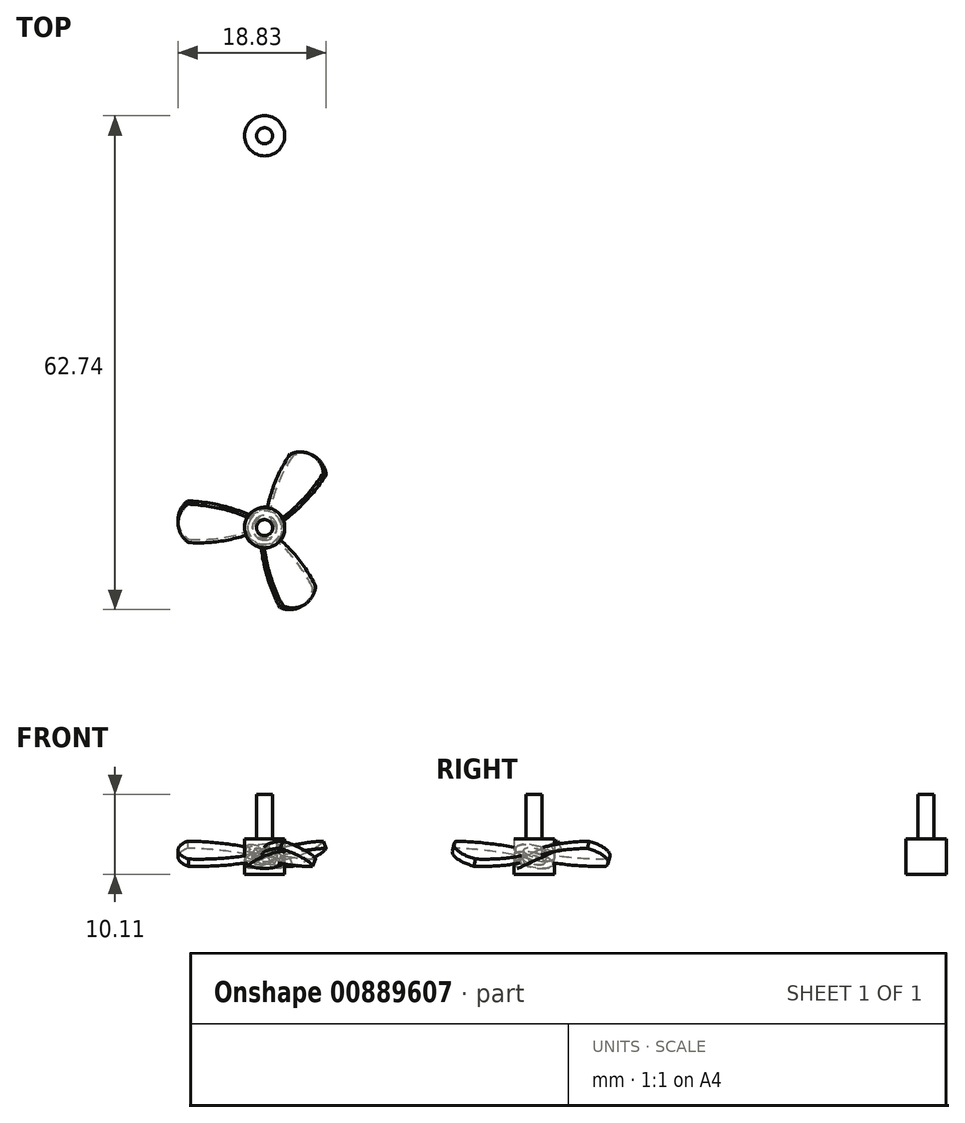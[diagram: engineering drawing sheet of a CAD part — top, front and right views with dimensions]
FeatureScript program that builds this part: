
annotation { "Feature Type Name" : "Feature", "Feature Type Description" : "" }
export const myFeature = defineFeature(function(context is Context, id is Id, definition is map)
    precondition{}
    {
        {
            var Q0;
            Q0=qCreatedBy(makeId("Top.planeOp"),FACE);
            var sketch = newSketch(context, id + "F0", { "sketchPlane" : qUnion([Q0])});
            skCircle(sketch, "E0", {"center": v(0, 0) * mm, "radius": 0.63 * mm});
            skCircle(sketch, "E1", {"center": v(0, 0) * mm, "radius": 1.5 * mm});
            skCircle(sketch, "E2.0", {"center": v(0, 0) * mm, "radius": 2.55 * mm});
            skPoint(sketch, "E3.center.orphan", {"position": v(-24.82, 0) * mm});
            skPoint(sketch, "E4.end.orphan", {"position": v(-27.48, 1.31) * mm});
            skPoint(sketch, "E4.start.orphan", {"position": v(-1.98, 1.6) * mm});
            skArc(sketch, "E5", {"start": v(-1.98, 1.6) * mm, "mid": v(-5.78, 2.95) * mm, "end": v(-9.77, 3.52) * mm});
            skArc(sketch, "E6", {"start": v(-9.68, -1.84) * mm, "mid": v(-6, -1.73) * mm, "end": v(-2.41, -0.83) * mm});
            skArc(sketch, "E7", {"start": v(-9.77, 3.52) * mm, "mid": v(-11, 0.82) * mm, "end": v(-9.68, -1.84) * mm});
            skSolve(sketch);
        }
        {
            var Q0;
            Q0=makeQuery(id+"F0.imprint","IMPRINT",FACE,{"disambiguationData":[TD([[makeQuery(id+"F0.imprint","IMPRINT",EDGE,{"derivedFrom":sQuery(id+"F0.wireOp",EDGE,"E1")}),-1.0]])]});
            var Q1;
            Q1=makeQuery(id+"F0.imprint","IMPRINT",FACE,{"disambiguationData":[TD([[makeQuery(id+"F0.imprint","IMPRINT",EDGE,{"derivedFrom":sQuery(id+"F0.wireOp",EDGE,"E0")}),-1.0]])]});
            var Q2;
            Q2=makeQuery(id+"F0.imprint","IMPRINT",FACE,{"disambiguationData":[TD([[makeQuery(id+"F0.imprint","IMPRINT",EDGE,{"derivedFrom":sQuery(id+"F0.wireOp",EDGE,"E0")}),1.0]])]});
            extrude(context, id + "F1", {"entities" : qUnion([Q0, Q1, Q2]), "endBound" : BoundingType.SYMMETRIC, "offsetDistance" : 25.4 * mm, "depth" : 4.5 * mm});
        }
        {
            var Q0;
            Q0 = qSketchRegion(id + "F0", true);
            extrude(context, id + "F2", {"entities" : qUnion([Q0]), "endBound" : BoundingType.SYMMETRIC, "offsetDistance" : 25.4 * mm, "depth" : 1 * mm});
        }
        {
            var Q0;
            Q0=qCreatedBy(makeId("Top.planeOp"),FACE);
            var sketch = newSketch(context, id + "F3", { "sketchPlane" : qUnion([Q0])});
            skLineSegment(sketch, "E8", {"start": v(7.03, 0) * mm, "end": v(-6.93, 0) * mm});
            skSolve(sketch);
        }
        {
            var Q0;
            Q0=makeQuery(id+"F2.opExtrude","SWEPT_BODY",BODY,{"disambiguationData":[OSD([sQuery(id+"F0.wireOp",EDGE,"E2.0"),sQuery(id+"F0.wireOp",EDGE,"E4"),sQuery(id+"F0.wireOp",EDGE,"E3"),sQuery(id+"F0.wireOp",EDGE,"psgykRgO-odCm-1AyA-wEhW-lGduvBCJNHCh")])]});
            var Q1;
            Q1=sQuery(id+"F3.wireOp",EDGE,"E8");
            transform(context, id + "F4", {"entities" : qUnion([Q0]), "transformType" : TransformType.ROTATION, "transformAxis" : qUnion([Q1]), "angle" : 25 * degree, "oppositeDirection" : true, "makeCopy" : false});
        }
        {
            var Q0;
            Q0=makeQuery(id+"F2.opExtrude","SWEPT_BODY",BODY,{"disambiguationData":[OSD([sQuery(id+"F0.wireOp",EDGE,"E2.0"),sQuery(id+"F0.wireOp",EDGE,"E4"),sQuery(id+"F0.wireOp",EDGE,"E3"),sQuery(id+"F0.wireOp",EDGE,"psgykRgO-odCm-1AyA-wEhW-lGduvBCJNHCh")])]});
            var Q1;
            Q1=sQuery(id+"F0.wireOp",EDGE,"E0");
            circularPattern(context, id + "F5", {"entities" : qUnion([Q0]), "axis" : qUnion([Q1]), "angle" : 360 * degree, "instanceCount" : 3, "equalSpace" : true});
        }
        {
            var Q0;
            Q0=makeQuery(id+"F5.opPattern","COPY",BODY,{"derivedFrom":makeQuery(id+"F2.opExtrude","SWEPT_BODY",BODY,{"disambiguationData":[OSD([sQuery(id+"F0.wireOp",EDGE,"E2.0"),sQuery(id+"F0.wireOp",EDGE,"E4"),sQuery(id+"F0.wireOp",EDGE,"E3"),sQuery(id+"F0.wireOp",EDGE,"psgykRgO-odCm-1AyA-wEhW-lGduvBCJNHCh")])]}),"instanceName":"1"});
            var Q1;
            Q1=makeQuery(id+"F5.opPattern","COPY",BODY,{"derivedFrom":makeQuery(id+"F2.opExtrude","SWEPT_BODY",BODY,{"disambiguationData":[OSD([sQuery(id+"F0.wireOp",EDGE,"E2.0"),sQuery(id+"F0.wireOp",EDGE,"E4"),sQuery(id+"F0.wireOp",EDGE,"E3"),sQuery(id+"F0.wireOp",EDGE,"psgykRgO-odCm-1AyA-wEhW-lGduvBCJNHCh")])]}),"instanceName":"2"});
            var Q2;
            Q2=makeQuery(id+"F2.opExtrude","SWEPT_BODY",BODY,{"disambiguationData":[OSD([sQuery(id+"F0.wireOp",EDGE,"E2.0"),sQuery(id+"F0.wireOp",EDGE,"E4"),sQuery(id+"F0.wireOp",EDGE,"E3"),sQuery(id+"F0.wireOp",EDGE,"psgykRgO-odCm-1AyA-wEhW-lGduvBCJNHCh")])]});
            var Q3;
            Q3=makeQuery(id+"F1.opExtrude","SWEPT_BODY",BODY,{"disambiguationData":[OSD([sQuery(id+"F0.wireOp",EDGE,"E1"),sQuery(id+"F0.wireOp",EDGE,"E2.0")])]});
            var Q4;
            Q4=qCreatedBy(makeId("Front.planeOp"),FACE);
            transform(context, id + "F6", {"entities" : qUnion([Q0, Q1, Q2, Q3]), "transformType" : TransformType.TRANSLATION_DISTANCE, "transformDirection" : qUnion([Q4]), "distance" : 25.4 * mm, "makeCopy" : false});
        }
        {
            var Q0;
            Q0=makeQuery(id+"F1.opExtrude","CAP_FACE",FACE,{"disambiguationData":[OSD([sQuery(id+"F0.wireOp",EDGE,"E1"),sQuery(id+"F0.wireOp",EDGE,"E2.0")])],"isStart":false});
            var sketch = newSketch(context, id + "F7", { "sketchPlane" : qUnion([Q0])});
            skCircle(sketch, "E9", {"center": v(0, -25.4) * mm, "radius": 0.75 * mm});
            skCircle(sketch, "E10", {"center": v(0, -25.4) * mm, "radius": 1.5 * mm});
            skSolve(sketch);
        }
        {
            var Q0;
            Q0=makeQuery(id+"F1.opExtrude","SWEPT_BODY",BODY,{"disambiguationData":[OSD([sQuery(id+"F0.wireOp",EDGE,"E1"),sQuery(id+"F0.wireOp",EDGE,"E2.0")])]});
            var Q1;
            Q1=makeQuery(id+"F2.opExtrude","SWEPT_BODY",BODY,{"disambiguationData":[OSD([sQuery(id+"F0.wireOp",EDGE,"E2.0"),sQuery(id+"F0.wireOp",EDGE,"E4"),sQuery(id+"F0.wireOp",EDGE,"E3"),sQuery(id+"F0.wireOp",EDGE,"psgykRgO-odCm-1AyA-wEhW-lGduvBCJNHCh")])]});
            var Q2;
            Q2=makeQuery(id+"F5.opPattern","COPY",BODY,{"derivedFrom":makeQuery(id+"F2.opExtrude","SWEPT_BODY",BODY,{"disambiguationData":[OSD([sQuery(id+"F0.wireOp",EDGE,"E2.0"),sQuery(id+"F0.wireOp",EDGE,"E4"),sQuery(id+"F0.wireOp",EDGE,"E3"),sQuery(id+"F0.wireOp",EDGE,"psgykRgO-odCm-1AyA-wEhW-lGduvBCJNHCh")])]}),"instanceName":"1"});
            var Q3;
            Q3=makeQuery(id+"F5.opPattern","COPY",BODY,{"derivedFrom":makeQuery(id+"F2.opExtrude","SWEPT_BODY",BODY,{"disambiguationData":[OSD([sQuery(id+"F0.wireOp",EDGE,"E2.0"),sQuery(id+"F0.wireOp",EDGE,"E4"),sQuery(id+"F0.wireOp",EDGE,"E3"),sQuery(id+"F0.wireOp",EDGE,"psgykRgO-odCm-1AyA-wEhW-lGduvBCJNHCh")])]}),"instanceName":"2"});
            var Q4;
            Q4=qCreatedBy(makeId("Front.planeOp"),FACE);
            mirror(context, id + "F8", {"entities" : qUnion([Q0, Q1, Q2, Q3]), "mirrorPlane" : qUnion([Q4])});
        }
        {
            var Q0;
            Q0=makeQuery(id+"F8.opPattern","COPY",BODY,{"derivedFrom":makeQuery(id+"F5.opPattern","COPY",BODY,{"derivedFrom":makeQuery(id+"F2.opExtrude","SWEPT_BODY",BODY,{"disambiguationData":[OSD([sQuery(id+"F0.wireOp",EDGE,"E2.0"),sQuery(id+"F0.wireOp",EDGE,"E4"),sQuery(id+"F0.wireOp",EDGE,"E3"),sQuery(id+"F0.wireOp",EDGE,"psgykRgO-odCm-1AyA-wEhW-lGduvBCJNHCh")])]}),"instanceName":"2"}),"instanceName":"1"});
            deleteBodies(context, id + "F9", {"entities" : qUnion([Q0])});
        }
        {
            var Q0;
            Q0=makeQuery(id+"F8.opPattern","COPY",BODY,{"derivedFrom":makeQuery(id+"F5.opPattern","COPY",BODY,{"derivedFrom":makeQuery(id+"F2.opExtrude","SWEPT_BODY",BODY,{"disambiguationData":[OSD([sQuery(id+"F0.wireOp",EDGE,"E2.0"),sQuery(id+"F0.wireOp",EDGE,"E4"),sQuery(id+"F0.wireOp",EDGE,"E3"),sQuery(id+"F0.wireOp",EDGE,"psgykRgO-odCm-1AyA-wEhW-lGduvBCJNHCh")])]}),"instanceName":"1"}),"instanceName":"1"});
            deleteBodies(context, id + "F10", {"entities" : qUnion([Q0])});
        }
        {
            var Q0;
            Q0=makeQuery(id+"F8.opPattern","COPY",BODY,{"derivedFrom":makeQuery(id+"F2.opExtrude","SWEPT_BODY",BODY,{"disambiguationData":[OSD([sQuery(id+"F0.wireOp",EDGE,"E2.0"),sQuery(id+"F0.wireOp",EDGE,"E4"),sQuery(id+"F0.wireOp",EDGE,"E3"),sQuery(id+"F0.wireOp",EDGE,"psgykRgO-odCm-1AyA-wEhW-lGduvBCJNHCh")])]}),"instanceName":"1"});
            deleteBodies(context, id + "F11", {"entities" : qUnion([Q0])});
        }
        {
            var Q0;
            Q0=makeQuery(id+"F8.opPattern","COPY",BODY,{"derivedFrom":makeQuery(id+"F1.opExtrude","SWEPT_BODY",BODY,{"disambiguationData":[OSD([sQuery(id+"F0.wireOp",EDGE,"E1"),sQuery(id+"F0.wireOp",EDGE,"E2.0")])]}),"instanceName":"1"});
            deleteBodies(context, id + "F12", {"entities" : qUnion([Q0])});
        }
        {
            var Q0;
            Q0=makeQuery(id+"F1.opExtrude","CAP_FACE",FACE,{"disambiguationData":[OSD([sQuery(id+"F0.wireOp",EDGE,"E2.0")])],"isStart":false});
            var sketch = newSketch(context, id + "F13", { "sketchPlane" : qUnion([Q0])});
            skCircle(sketch, "E11", {"center": v(0, -25.4) * mm, "radius": 1.02 * mm});
            skSolve(sketch);
        }
        {
            var Q0;
            Q0=makeQuery(id+"F13.imprint","IMPRINT",FACE,{"disambiguationData":[TD([[makeQuery(id+"F13.imprint","IMPRINT",EDGE,{"derivedFrom":sQuery(id+"F13.wireOp",EDGE,"E11")}),1.0]])]});
            extrude(context, id + "F14", {"entities" : qUnion([Q0]), "operationType" : NewBodyOperationType.ADD, "depth" : 5.61 * mm, "offsetDistance" : 25.4 * mm});
        }
        {
            var Q0;
            Q0=makeQuery(id+"F1.opExtrude","SWEPT_BODY",BODY,{"disambiguationData":[OSD([sQuery(id+"F0.wireOp",EDGE,"E2.0")])]});
            transform(context, id + "F15", {"entities" : qUnion([Q0]), "transformType" : TransformType.TRANSLATION_3D, "dx" : 0 * mm, "dy" : 49.78 * mm, "dz" : 0 * mm, "makeCopy" : true});
        }
    });
